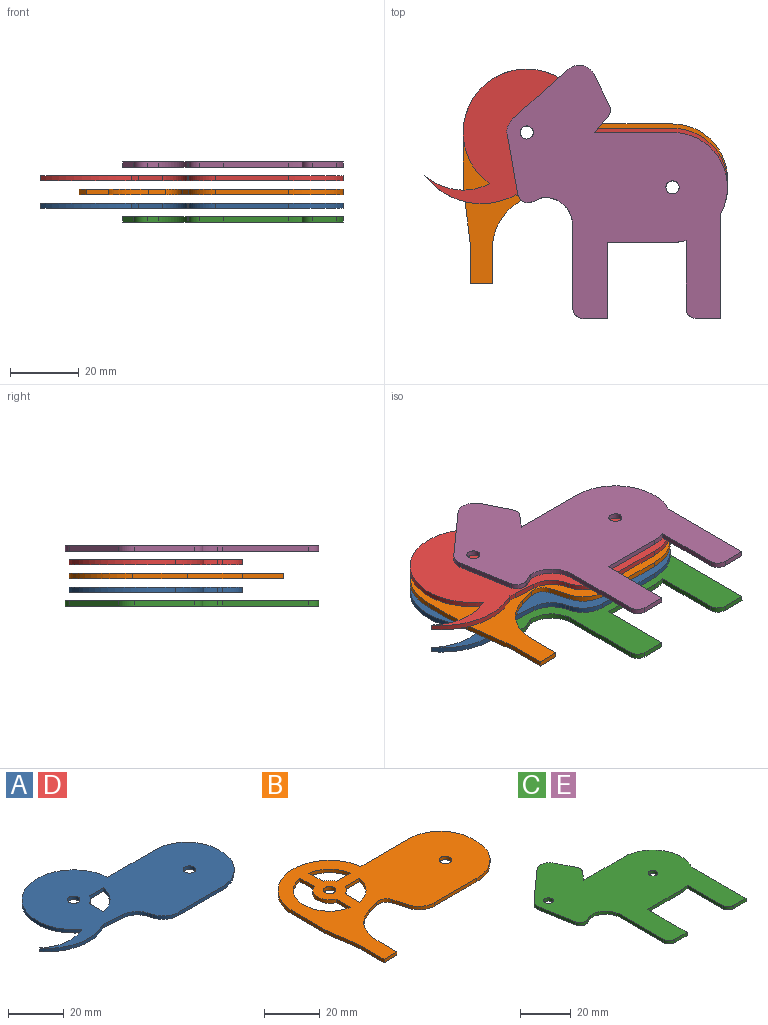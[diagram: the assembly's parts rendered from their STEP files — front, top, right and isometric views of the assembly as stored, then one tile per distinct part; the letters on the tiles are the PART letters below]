
ASSEMBLY  parts=5 mates=4
PART A: 21 faces, bbox 88.3x50.5x1.5 mm
  f0: cylinder r=13mm len=10.55mm, axis (0,0,-1), area 23.8mm2, adj f1,f18,f19,f20
  f1: plane 7.24x1.5mm, normal (1,0,0), area 10.9mm2, adj f0,f2,f19,f20
  f2: cylinder r=6mm len=3.31mm, axis (0,0,-1), area 7.2mm2, adj f1,f18,f19,f20
  f3: cylinder r=20.74mm len=26.5mm, axis (0,0,-1), area 44.3mm2, adj f4,f17,f19,f20
  f4: cylinder r=18.5mm len=2.03mm, axis (0,0,-1), area 3.1mm2, adj f3,f5,f19,f20
  f5: plane 7.12x1.5mm, normal (-0.07,-1,0), area 10.7mm2, adj f4,f6,f19,f20
  f6: cylinder r=8mm len=7.17mm, axis (0,0,-1), area 14.8mm2, adj f5,f7,f19,f20
  f7: plane 1.5x1.42mm, normal (-0.96,-0.27,0), area 2.2mm2, adj f6,f8,f19,f20
  f8: cylinder r=8mm len=7.7mm, axis (0,0,-1), area 15.6mm2, adj f7,f9,f19,f20
  f9: plane 21.34x1.5mm, normal (0,-1,0), area 32mm2, adj f8,f10,f19,f20
  f10: cylinder r=16mm len=16mm, axis (0,0,-1), area 37.7mm2, adj f9,f11,f19,f20
  f11: plane 1.5x1.25mm, normal (1,0,0), area 1.9mm2, adj f10,f12,f19,f20
  f12: cylinder r=16mm len=16mm, axis (0,0,-1), area 37.7mm2, adj f11,f13,f19,f20
  f13: plane 24.04x1.5mm, normal (0,1,0), area 36.1mm2, adj f12,f14,f19,f20
  f14: cylinder r=18.5mm len=36.96mm, axis (0,0,-1), area 111.5mm2, adj f13,f17,f19,f20
  f15: cylinder r=2.25mm len=4.5mm, axis (0,0,-1), area 21.2mm2, adj f19,f20
  f16: cylinder r=2.25mm len=4.5mm, axis (0,0,-1), area 21.2mm2, adj f19,f20
  f17: cylinder r=16.8mm len=18.89mm, axis (0,0,-1), area 30.4mm2, adj f3,f14,f19,f20
  f18: plane 7.24x1.5mm, normal (0,-1,0), area 10.9mm2, adj f0,f2,f19,f20
  f19: plane 88.26x50.5mm, normal (0,0,1), area 2413.5mm2, adj f0,f1,f2,f3,f4,f5,f6,f7
  f20: plane 88.26x50.5mm, normal (0,0,-1), area 2413.5mm2, adj f0,f1,f2,f3,f4,f5,f6,f7
PART B: 32 faces, bbox 77x62.5x1.5 mm
  f0: plane 10.09x1.5mm, normal (1,0,0), area 15.1mm2, adj f1,f29,f30,f31
  f1: cylinder r=16mm len=15.4mm, axis (0,0,-1), area 31.1mm2, adj f0,f2,f30,f31
  f2: plane 5.07x1.5mm, normal (0.27,-0.96,0), area 7.9mm2, adj f1,f3,f30,f31
  f3: cylinder r=4mm len=4.94mm, axis (0,0,-1), area 9.4mm2, adj f2,f4,f30,f31
  f4: plane 6.32x1.78mm, normal (-0.96,-0.27,0), area 9.8mm2, adj f3,f5,f30,f31
  f5: cylinder r=8mm len=7.7mm, axis (0,0,-1), area 15.6mm2, adj f4,f6,f30,f31
  f6: plane 21.34x1.5mm, normal (0,-1,0), area 32mm2, adj f5,f7,f30,f31
  f7: cylinder r=16mm len=16mm, axis (0,0,-1), area 37.7mm2, adj f6,f8,f30,f31
  f8: plane 2.5x1.5mm, normal (1,0,0), area 3.8mm2, adj f7,f9,f30,f31
  f9: cylinder r=16mm len=16mm, axis (0,0,-1), area 37.7mm2, adj f8,f10,f30,f31
  f10: plane 24.17x1.5mm, normal (0,1,0), area 36.3mm2, adj f9,f11,f30,f31
  f11: cylinder r=18.5mm len=36.83mm, axis (0,0,-1), area 83.4mm2, adj f10,f12,f30,f31
  f12: plane 16x1.5mm, normal (-1,0,0), area 24mm2, adj f11,f13,f30,f31
  f13: plane 16x2.01mm, normal (-0.99,-0.12,0), area 24.2mm2, adj f12,f14,f30,f31
  f14: plane 12x1.5mm, normal (-1,0,0), area 18mm2, adj f13,f29,f30,f31
  f15: cylinder r=13mm len=25.61mm, axis (0,0,-1), area 54.5mm2, adj f16,f24,f30,f31
  f16: plane 7.24x1.5mm, normal (-1,0,0), area 10.9mm2, adj f15,f17,f30,f31
  f17: cylinder r=6mm len=11.12mm, axis (0,0,-1), area 21.4mm2, adj f16,f24,f30,f31
  f18: plane 7.24x1.5mm, normal (1,0,0), area 10.9mm2, adj f19,f25,f30,f31
  f19: cylinder r=6mm len=3.31mm, axis (0,0,-1), area 7.2mm2, adj f18,f20,f30,f31
  f20: plane 7.24x1.5mm, normal (0,-1,0), area 10.9mm2, adj f19,f25,f30,f31
  f21: plane 7.24x1.5mm, normal (0,1,0), area 10.9mm2, adj f22,f26,f30,f31
  f22: cylinder r=6mm len=3.31mm, axis (0,0,-1), area 7.2mm2, adj f21,f23,f30,f31
  f23: plane 7.24x1.5mm, normal (1,0,0), area 10.9mm2, adj f22,f26,f30,f31
  f24: plane 7.24x1.5mm, normal (-1,0,0), area 10.9mm2, adj f15,f17,f30,f31
  f25: cylinder r=13mm len=10.55mm, axis (0,0,-1), area 23.8mm2, adj f18,f20,f30,f31
  f26: cylinder r=13mm len=10.55mm, axis (0,0,-1), area 23.8mm2, adj f21,f23,f30,f31
  f27: cylinder r=2.25mm len=4.5mm, axis (0,0,-1), area 21.2mm2, adj f30,f31
  f28: cylinder r=2.25mm len=4.5mm, axis (0,0,-1), area 21.2mm2, adj f30,f31
  f29: plane 6.5x1.5mm, normal (0,-1,0), area 9.7mm2, adj f0,f14,f30,f31
  f30: plane 77x62.5mm, normal (0,0,1), area 2418.4mm2, adj f0,f1,f2,f3,f4,f5,f6,f7
  f31: plane 77x62.5mm, normal (0,0,-1), area 2418.4mm2, adj f0,f1,f2,f3,f4,f5,f6,f7
PART C: 27 faces, bbox 64.3x73.8x1.5 mm
  f0: plane 7x1.5mm, normal (0,-1,0), area 10.5mm2, adj f1,f23,f25,f26
  f1: plane 30.41x1.5mm, normal (1,0,0), area 45.6mm2, adj f0,f2,f25,f26
  f2: cylinder r=16mm len=23.82mm, axis (0,0,-1), area 50mm2, adj f1,f3,f25,f26
  f3: plane 22.74x1.5mm, normal (0,1,0), area 34.1mm2, adj f2,f4,f25,f26
  f4: plane 4.71x3.96mm, normal (0.77,-0.64,0), area 9.2mm2, adj f3,f5,f25,f26
  f5: cylinder r=3mm len=3.27mm, axis (0,0,-1), area 5.2mm2, adj f4,f6,f25,f26
  f6: plane 8.81x4.38mm, normal (0.9,0.45,0), area 14.8mm2, adj f5,f7,f25,f26
  f7: cylinder r=5mm len=7.81mm, axis (0,0,-1), area 13.8mm2, adj f6,f8,f25,f26
  f8: plane 16.01x14.31mm, normal (-0.67,0.75,0), area 32.2mm2, adj f7,f9,f25,f26
  f9: cylinder r=5mm len=4.61mm, axis (0,0,-1), area 7.6mm2, adj f8,f10,f25,f26
  f10: plane 17.37x3.1mm, normal (-0.98,-0.18,0), area 26.5mm2, adj f9,f11,f25,f26
  f11: cylinder r=3mm len=4.11mm, axis (0,0,-1), area 8.1mm2, adj f10,f12,f25,f26
  f12: plane 3.07x1.5mm, normal (0.39,-0.92,0), area 5mm2, adj f11,f13,f25,f26
  f13: cylinder r=8mm len=8.45mm, axis (0,0,-1), area 16.7mm2, adj f12,f14,f25,f26
  f14: plane 1.5x1.42mm, normal (-0.96,-0.27,0), area 2.2mm2, adj f13,f15,f25,f26
  f15: plane 25.06x1.5mm, normal (-1,0,0), area 37.6mm2, adj f14,f16,f25,f26
  f16: cylinder r=3mm len=3mm, axis (0,0,-1), area 7.1mm2, adj f15,f17,f25,f26
  f17: plane 7x1.5mm, normal (0,-1,0), area 10.5mm2, adj f16,f18,f25,f26
  f18: plane 22.23x1.5mm, normal (1,0,0), area 33.3mm2, adj f17,f19,f25,f26
  f19: plane 19.04x1.5mm, normal (0,-1,0), area 28.6mm2, adj f18,f20,f25,f26
  f20: cylinder r=16mm len=3.96mm, axis (0,0,-1), area 6mm2, adj f19,f21,f25,f26
  f21: plane 19.73x1.5mm, normal (-1,0,0), area 29.6mm2, adj f20,f23,f25,f26
  f22: cylinder r=1.91mm len=3.81mm, axis (0,0,-1), area 18mm2, adj f25,f26
  f23: cylinder r=3mm len=3mm, axis (0,0,-1), area 7.1mm2, adj f0,f21,f25,f26
  f24: cylinder r=1.91mm len=3.81mm, axis (0,0,-1), area 18mm2, adj f25,f26
  f25: plane 73.79x64.26mm, normal (0,0,1), area 2509.4mm2, adj f0,f1,f2,f3,f4,f5,f6,f7
  f26: plane 73.79x64.26mm, normal (0,0,-1), area 2509.4mm2, adj f0,f1,f2,f3,f4,f5,f6,f7
PART D: same geometry as A
PART E: same geometry as C
PLACE A t=(-66.99,11.47,-0.09)mm
PLACE B t=(18.36,11.01,7.41)mm
PLACE C t=(-44.16,63.01,-4.09)mm
PLACE D t=(-66.99,11.47,7.91)mm
PLACE E t=(-44.16,63.01,11.91)mm
MATE fastened D.f0 <-> B.f11  axis (0,0,1) through (-0.29,24.73,12.91)mm
MATE fastened C.f2 <-> A.f10  axis (0,0,-1) through (42.21,8.73,-0.59)mm
MATE fastened E.f2 <-> D.f10  axis (0,0,1) through (42.21,8.73,16.91)mm
MATE fastened A.f0 <-> B.f11  axis (0,0,1) through (-0.29,24.73,4.91)mm
